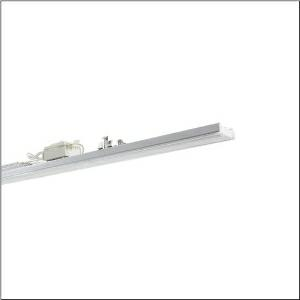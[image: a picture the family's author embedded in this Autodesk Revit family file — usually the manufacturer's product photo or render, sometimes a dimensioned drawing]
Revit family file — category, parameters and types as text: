
# Revit family: licross_11_recessed_mo_51tl12dnd9xg
name_source: partatom
category: Lighting Fixtures
units: mm (PartAtom-declared; Revit-internal decimal feet)

## family parameters
Cut with Voids When Loaded = No
Host = Face
Light Source = No
Part Type = Normal
Room Calculation Point = No
Round Connector Dimension = Use Diameter
Shared = No

## types (1)
- --- (1 x LED, 9310 lm, 56.2 W, 4000K)
    Apparent Load = 56 VA
    CIE Flux Codes = 67 92 99 100 100
    Color Rendering = 90
    Color Temperature = 4000K
    Default Elevation = 1800 mm
    Description = Licross 11 Recessed MO, luminaire insert, of sheet steel, coil coated, white, length: 1.500mm, width: 66mm, height: 67mm, LED rated luminous flux: 9.310lm, light colour: 940, SDCM (Standard Deviation of Colour Matching)MacAdam ≤ 2 SDCM (initial), control gear: DALI 2, with plug, 5-pole, with phase selection, mains connection: 220..240V, AC, 50/60Hz, rated input power: 56W, internal wiring halogen-free, primary optical cover: cover, of PMMA, light emission: direct distribution, primary light characteristic: symmetric, protection rating (complete): IP40, insulation class (complete): insulation class I (protective earthing), certification: CE, ENEC, VDE, UKCA, protection symbol: D if used in an environment without relevant dust loads with corresponding accessories, impact resistance: IK06, permissible ambient temperature for indoor applications: -25..+45°C, corresponds to IFS (International Featured Standards) requirements for safety and quality in the food industry, reducing of maximum allowable ambient temperature of 5°C with ceiling mounting, LABS conformity tested according to VDMA 24364:2018-05, The light source and the operating device comply with the requirements of the Ecodesign Regulation (EU) 2019/2020 and are replaceable in accordance with this regulation, packaging unit: 1 piece
    Height = 58 mm
    Lamp = 1 x LED
    Lamp Light Flux = 9310 lm
    Lamp Power = 56.2 W
    Lamp count = 1
    Length = 1500 mm
    Luminous efficacy = 166 lm/W
    Manufacturer = Siteco
    ModVariant = No
    Model = 51TL12DND9XG
    Mounting Place = Ceiling
    Mounting Type = Pendant
    Number of Poles = 1
    OnlyDefault = Yes
    Power Factor = 1
    Product Name = Licross 11 Recessed MO
    Product group = luminaire insert | ceiling pendant
    ProductGroupID = 901
    Protection Class = Protection class I
    Protection Degree = IP 40
    RLX_Detail_Level = 1
    RLX_Emergency_Light_Flux = 0 lm
    RLX_Emergency_Type = 0
    RLX_Emergency_Type_DB = No
    RlxData = <blob elided: 24761 chars, md5=36308dfe>
    Socket = socket
    Standby Power = 0 W
    System Light Flux = 9310 lm
    System Power = 56 W
    Type Comments = factory setting: luminous flux: 100 % | dim-lin: 254 | 378 mA
    Type Image = l_1296930.jpg
    URL = http://relux.com
    VarID = @adj_056073
    Voltage = 0 V
    Weight = 0.00 kg
    Width = 66 mm

## geometry (parser evidence)
native form markers: Blend x4, Sweep x11
no freeform markers — native parametric forms only
